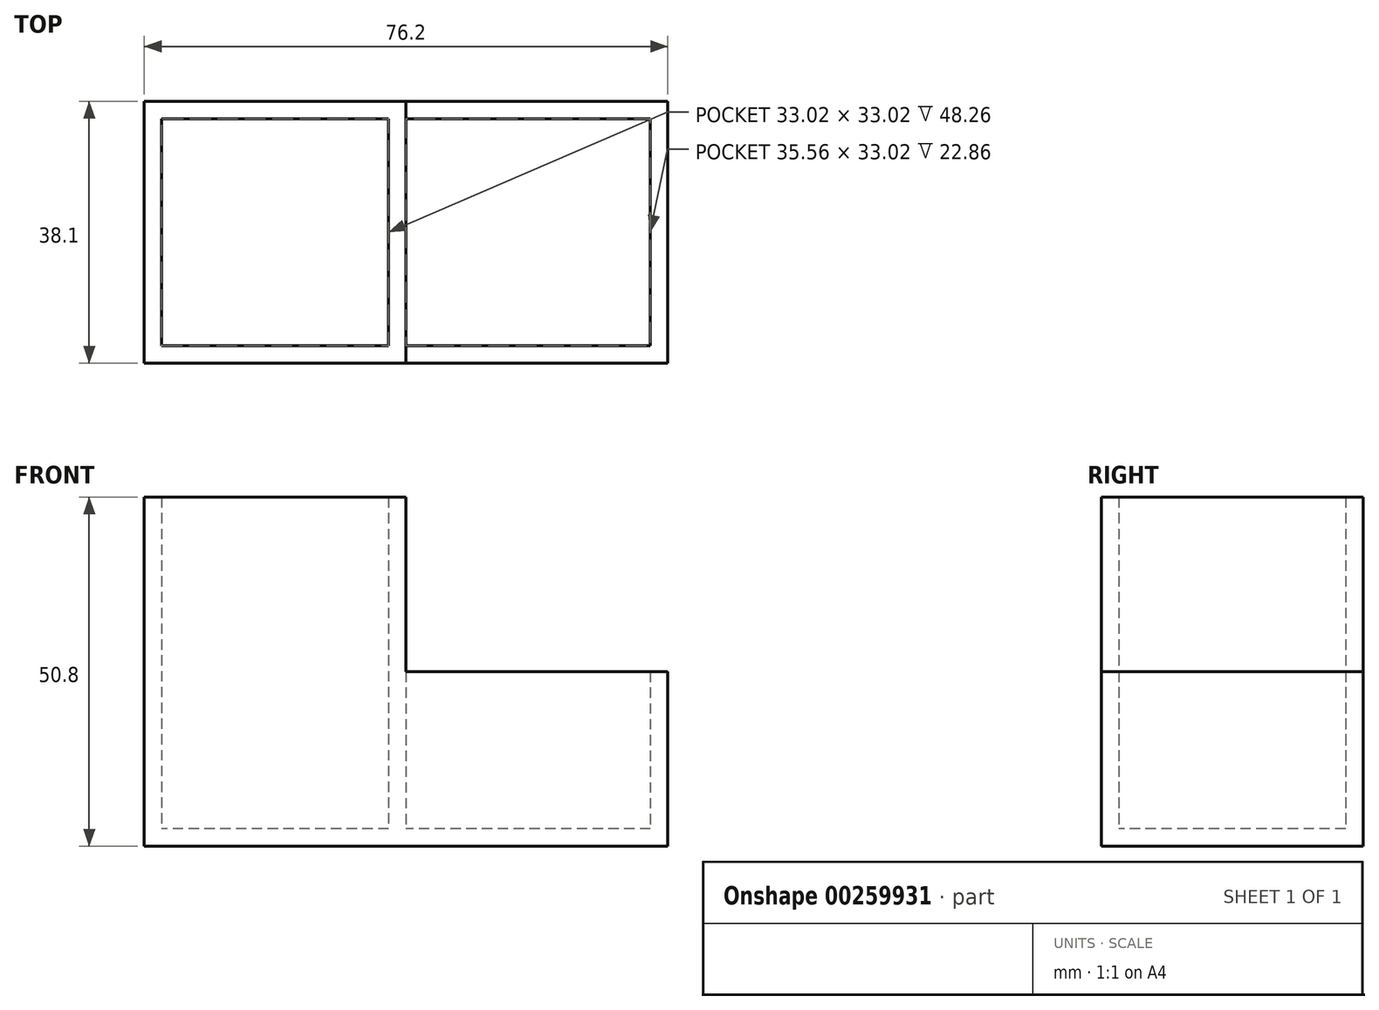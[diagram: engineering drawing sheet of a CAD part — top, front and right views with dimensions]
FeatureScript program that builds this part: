
annotation { "Feature Type Name" : "Feature", "Feature Type Description" : "" }
export const myFeature = defineFeature(function(context is Context, id is Id, definition is map)
    precondition{}
    {
        {
            var Q0;
            Q0=qCreatedBy(makeId("Top.planeOp"),FACE);
            var sketch = newSketch(context, id + "F0", { "sketchPlane" : qUnion([Q0])});
            skLineSegment(sketch, "E0.bottom", {"start": v(19.05, 19.05) * mm, "end": v(-19.05, 19.05) * mm});
            skLineSegment(sketch, "E0.top", {"start": v(19.05, -19.05) * mm, "end": v(-19.05, -19.05) * mm});
            skLineSegment(sketch, "E0.left", {"start": v(19.05, 19.05) * mm, "end": v(19.05, -19.05) * mm});
            skLineSegment(sketch, "E0.right", {"start": v(-19.05, 19.05) * mm, "end": v(-19.05, -19.05) * mm});
            skPoint(sketch, "E0.middle", {"position": v(0, 0) * mm});
            skLineSegment(sketch, "E1.bottom", {"start": v(19.05, -19.05) * mm, "end": v(57.15, -19.05) * mm});
            skLineSegment(sketch, "E1.top", {"start": v(19.05, 19.05) * mm, "end": v(57.15, 19.05) * mm});
            skLineSegment(sketch, "E1.left", {"start": v(19.05, -19.05) * mm, "end": v(19.05, 19.05) * mm});
            skLineSegment(sketch, "E1.right", {"start": v(57.15, -19.05) * mm, "end": v(57.15, 19.05) * mm});
            skSolve(sketch);
        }
        {
            var Q0;
            Q0=makeQuery(id+"F0.imprint","IMPRINT",FACE,{"disambiguationData":[TD([[makeQuery(id+"F0.imprint","IMPRINT",EDGE,{"derivedFrom":sQuery(id+"F0.wireOp",EDGE,"E0.bottom")}),1.0]])]});
            extrude(context, id + "F1", {"entities" : qUnion([Q0]), "depth" : 50.8 * mm});
        }
        {
            var Q0;
            Q0=makeQuery(id+"F1.opExtrude","CAP_FACE",FACE,{"disambiguationData":[OSD([sQuery(id+"F0.wireOp",EDGE,"E0.bottom"),sQuery(id+"F0.wireOp",EDGE,"E0.top"),sQuery(id+"F0.wireOp",EDGE,"E0.left"),sQuery(id+"F0.wireOp",EDGE,"E0.right")])],"isStart":false});
            shell(context, id + "F2", {"entities" : qUnion([Q0]), "thickness" : 2.54 * mm});
        }
        {
            var Q0;
            Q0=makeQuery(id+"F0.imprint","IMPRINT",FACE,{"disambiguationData":[TD([[makeQuery(id+"F0.imprint","IMPRINT",EDGE,{"derivedFrom":sQuery(id+"F0.wireOp",EDGE,"E1.bottom")}),1.0]])]});
            extrude(context, id + "F3", {"entities" : qUnion([Q0]), "operationType" : NewBodyOperationType.ADD, "depth" : 25.4 * mm});
        }
        {
            var Q0;
            Q0=makeQuery(id+"F3.opExtrude","CAP_FACE",FACE,{"disambiguationData":[OSD([sQuery(id+"F0.wireOp",EDGE,"E1.bottom"),sQuery(id+"F0.wireOp",EDGE,"E1.top"),sQuery(id+"F0.wireOp",EDGE,"E1.left"),sQuery(id+"F0.wireOp",EDGE,"E1.right")])],"isStart":false});
            shell(context, id + "F4", {"entities" : qUnion([Q0]), "thickness" : 2.54 * mm});
        }
    });
